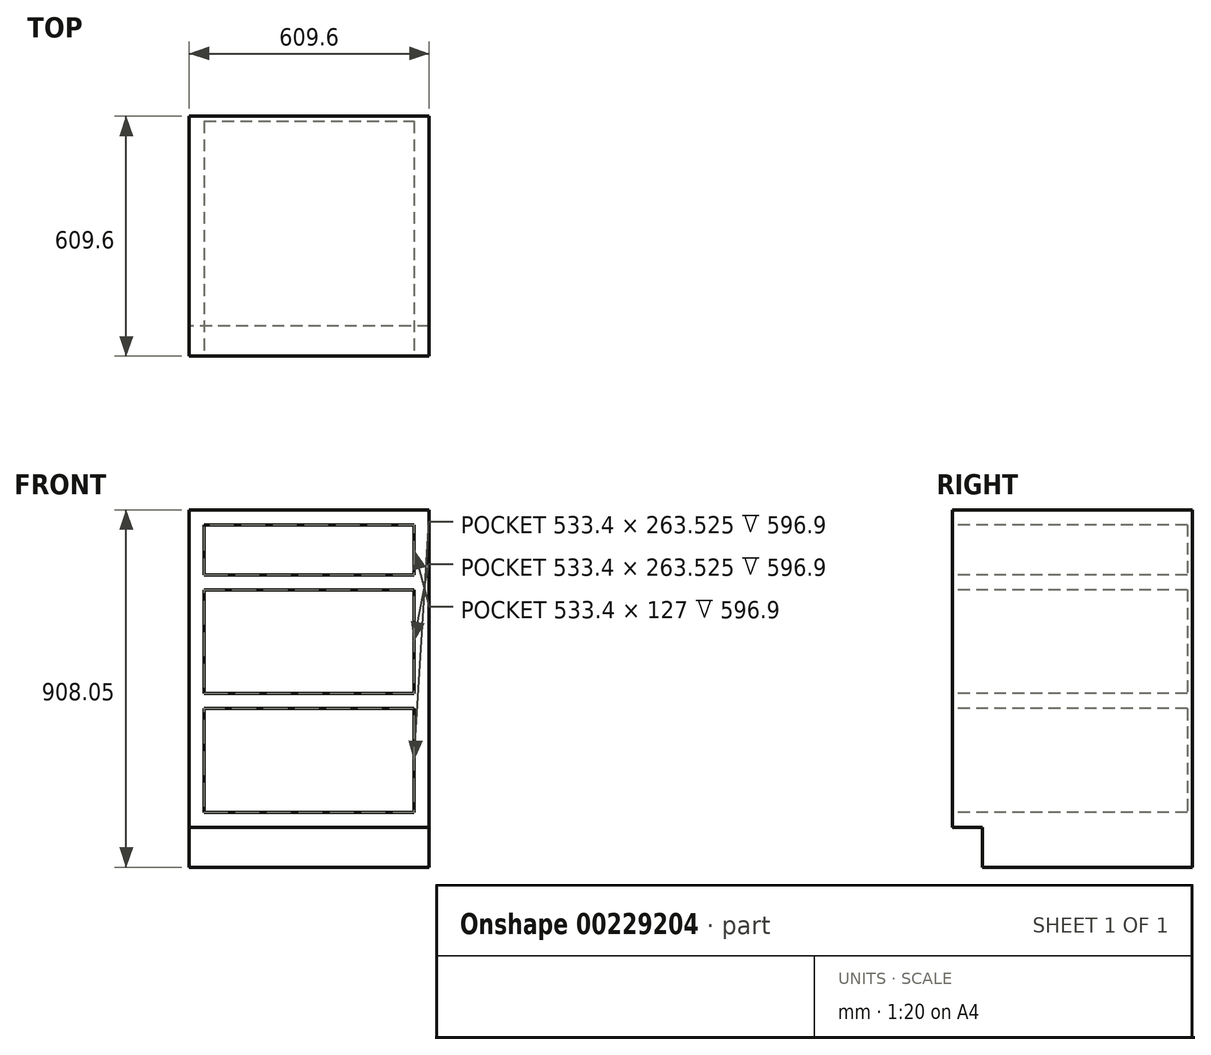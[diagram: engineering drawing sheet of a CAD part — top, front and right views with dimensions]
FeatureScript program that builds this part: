
annotation { "Feature Type Name" : "Feature", "Feature Type Description" : "" }
export const myFeature = defineFeature(function(context is Context, id is Id, definition is map)
    precondition{}
    {
        {
            var Q0;
            Q0=qCreatedBy(makeId("Right.planeOp"),FACE);
            var sketch = newSketch(context, id + "F0", { "sketchPlane" : qUnion([Q0])});
            skLineSegment(sketch, "E0", {"start": v(0, 0) * mm, "end": v(-533.4, 0) * mm});
            skLineSegment(sketch, "E1", {"start": v(-533.4, 0) * mm, "end": v(-533.4, 101.6) * mm});
            skLineSegment(sketch, "E2", {"start": v(-533.4, 101.6) * mm, "end": v(-609.6, 101.6) * mm});
            skLineSegment(sketch, "E3", {"start": v(-609.6, 101.6) * mm, "end": v(-609.6, 908.05) * mm});
            skLineSegment(sketch, "E4", {"start": v(-609.6, 908.05) * mm, "end": v(0, 908.05) * mm});
            skLineSegment(sketch, "E5", {"start": v(0, 908.05) * mm, "end": v(0, 0) * mm});
            skSolve(sketch);
        }
        {
            var Q0;
            Q0=makeQuery(id+"F0.imprint","IMPRINT",FACE,{"disambiguationData":[TD([[makeQuery(id+"F0.imprint","IMPRINT",EDGE,{"derivedFrom":sQuery(id+"F0.wireOp",EDGE,"E0")}),-1.0]])]});
            extrude(context, id + "F1", {"entities" : qUnion([Q0]), "depth" : 609.6 * mm});
        }
        {
            var Q0;
            Q0=makeQuery(id+"F1.opExtrude","SWEPT_FACE",FACE,{"disambiguationData":[OSD([sQuery(id+"F0.wireOp",EDGE,"E3")])]});
            var sketch = newSketch(context, id + "F2", { "sketchPlane" : qUnion([Q0])});
            skLineSegment(sketch, "E6.bottom", {"start": v(38.1, 869.95) * mm, "end": v(571.5, 869.95) * mm});
            skLineSegment(sketch, "E6.top", {"start": v(38.1, 742.95) * mm, "end": v(571.5, 742.95) * mm});
            skLineSegment(sketch, "E6.left", {"start": v(38.1, 869.95) * mm, "end": v(38.1, 742.95) * mm});
            skLineSegment(sketch, "E6.right", {"start": v(571.5, 869.95) * mm, "end": v(571.5, 742.95) * mm});
            skLineSegment(sketch, "E7.bottom", {"start": v(38.1, 704.85) * mm, "end": v(571.5, 704.85) * mm});
            skLineSegment(sketch, "E7.top", {"start": v(38.1, 441.33) * mm, "end": v(571.5, 441.33) * mm});
            skLineSegment(sketch, "E7.left", {"start": v(38.1, 704.85) * mm, "end": v(38.1, 441.33) * mm});
            skLineSegment(sketch, "E7.right", {"start": v(571.5, 704.85) * mm, "end": v(571.5, 441.33) * mm});
            skLineSegment(sketch, "E8.bottom", {"start": v(38.1, 403.23) * mm, "end": v(571.5, 403.23) * mm});
            skLineSegment(sketch, "E8.top", {"start": v(38.1, 139.7) * mm, "end": v(571.5, 139.7) * mm});
            skLineSegment(sketch, "E8.left", {"start": v(38.1, 403.23) * mm, "end": v(38.1, 139.7) * mm});
            skLineSegment(sketch, "E8.right", {"start": v(571.5, 403.23) * mm, "end": v(571.5, 139.7) * mm});
            skSolve(sketch);
        }
        {
            var Q0;
            Q0=makeQuery(id+"F2.imprint","IMPRINT",FACE,{"disambiguationData":[TD([[makeQuery(id+"F2.imprint","IMPRINT",EDGE,{"derivedFrom":sQuery(id+"F2.wireOp",EDGE,"E6.bottom")}),-1.0]])]});
            var Q1;
            Q1=makeQuery(id+"F2.imprint","IMPRINT",FACE,{"disambiguationData":[TD([[makeQuery(id+"F2.imprint","IMPRINT",EDGE,{"derivedFrom":sQuery(id+"F2.wireOp",EDGE,"E7.bottom")}),-1.0]])]});
            var Q2;
            Q2=makeQuery(id+"F2.imprint","IMPRINT",FACE,{"disambiguationData":[TD([[makeQuery(id+"F2.imprint","IMPRINT",EDGE,{"derivedFrom":sQuery(id+"F2.wireOp",EDGE,"E8.bottom")}),-1.0]])]});
            var Q3;
            Q3=makeQuery(id+"F2.imprint","IMPRINT",FACE,{"disambiguationData":[TD([[makeQuery(id+"F2.imprint","IMPRINT",EDGE,{"derivedFrom":sQuery(id+"F2.wireOp",EDGE,"z5dql7AH-9pPf-yf0r-Lgpp-hoX97IjUhxXj.bottom")}),-1.0]])]});
            extrude(context, id + "F3", {"entities" : qUnion([Q0, Q1, Q2, Q3]), "operationType" : NewBodyOperationType.REMOVE, "oppositeDirection" : true, "depth" : 596.9 * mm});
        }
    });
